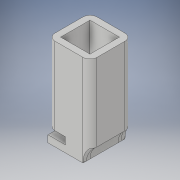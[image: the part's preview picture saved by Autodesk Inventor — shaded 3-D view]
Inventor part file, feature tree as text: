
AUTODESK INVENTOR PART (.ipt)
format: ipt  version: 2019.4 (Build 234330000, 330)  size: 202,752 bytes
history: native  units: mm
features: extrude x6, sketch x6, fillet x3
ambient origin geometry x8: Origin, YZ Plane, XZ Plane, XY Plane, X Axis, Y Axis, Z Axis, Center Point
bodies: Solid1 (feature_tree)
feature tree (15):
  extrude  "Extrusion1"  Depth=30.0mm
  extrude  "Extrusion2"  Depth=4.5mm
  extrude  "Extrusion3"  Depth=21.0mm
  fillet  "Fillet2"  Radius=21.0mm
  extrude  "Extrusion4"  Depth=15.0mm
  fillet  "Fillet3"  Radius=4.0mm
  extrude  "Extrusion5"  Depth=10.0mm
  fillet  "Fillet4"  Radius=10.0mm
  extrude  "Extrusion6"  TaperAngle=0.0deg  [1 undecoded]
  sketch  "Sketch1"  dims[d0=30.0mm d1=30.0mm]
  sketch  "Sketch2"  dims[d2=55.4mm d3=0.0mm d4=4.5mm]
  sketch  "Sketch3"  dims[d5=4.5mm d6=21.0mm d7=21.0mm]
  sketch  "Sketch4"  dims[d8=30.0mm d9=0.0mm d10=15.0mm d11=4.0mm]
  sketch  "Sketch5"  dims[d12=5.0mm d13=0.0mm d15=5.0mm d16=10.0mm]
  sketch  "Sketch6"  dims[d17=6.0mm d18=0.0mm d19=120.0deg d20=5.0mm d21=0.0mm d22=5.0mm d23=25.0mm d24=30.0mm d25=5.0mm d26=0.0mm d27=13.0mm d29=4.0mm d30=5.0mm d31=0.0mm]
note: 1 required parameter value undecoded (feature->parameter linkage not recoverable at this tier; creation-order binding heuristic only, values carry confidence <= 0.55)
